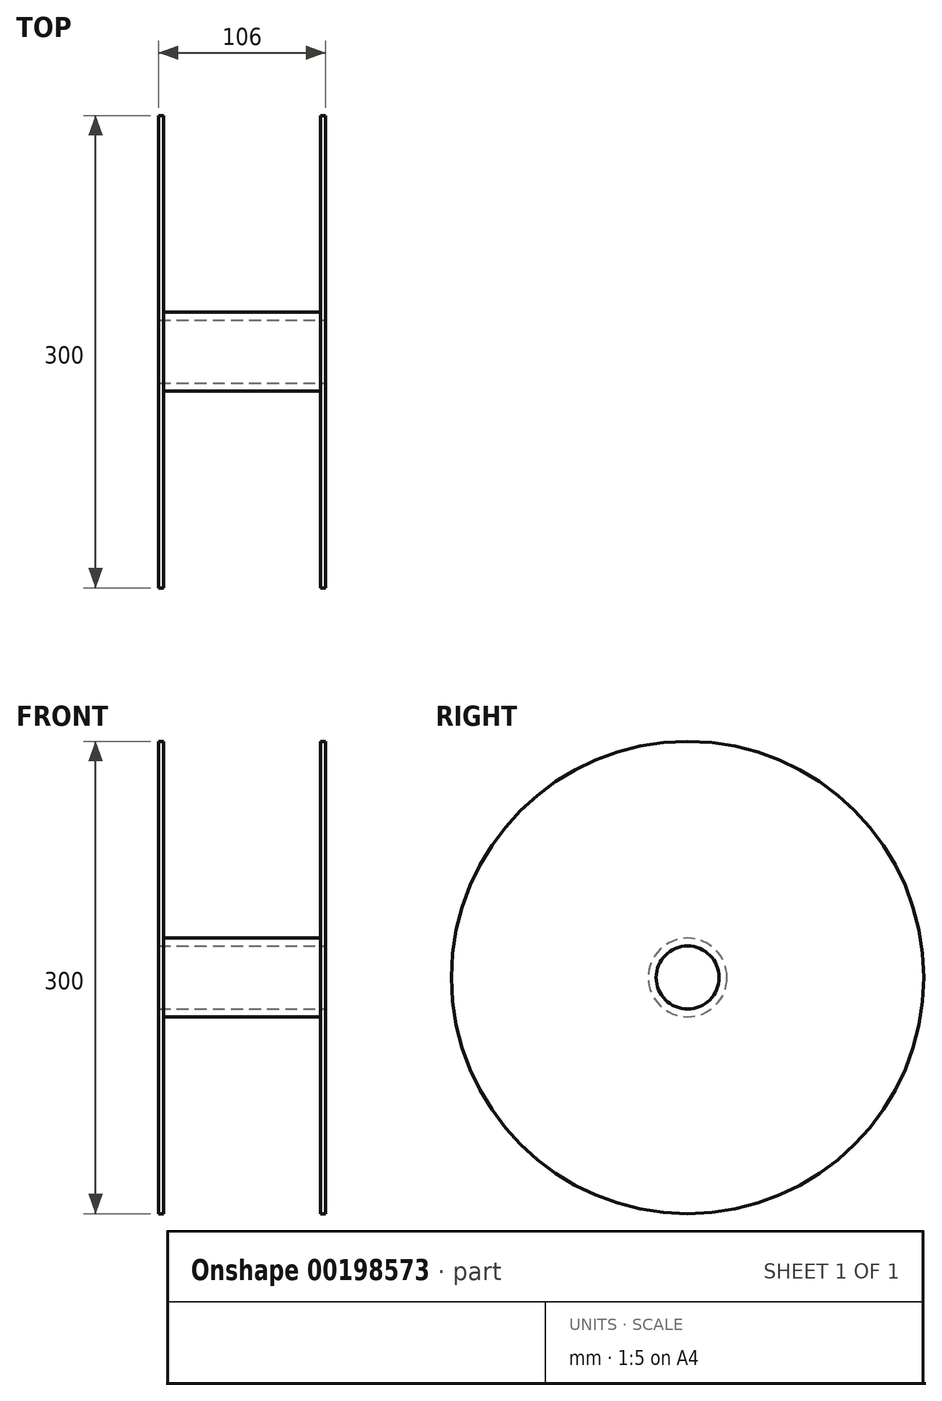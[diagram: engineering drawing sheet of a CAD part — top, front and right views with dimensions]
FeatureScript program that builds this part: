
annotation { "Feature Type Name" : "Feature", "Feature Type Description" : "" }
export const myFeature = defineFeature(function(context is Context, id is Id, definition is map)
    precondition{}
    {
        {
            var Q0;
            Q0=qCreatedBy(makeId("Front.planeOp"),FACE);
            var sketch = newSketch(context, id + "F0", { "sketchPlane" : qUnion([Q0])});
            skLineSegment(sketch, "E0", {"start": v(0, 25) * mm, "end": v(50, 25) * mm});
            skLineSegment(sketch, "E1", {"start": v(50, 25) * mm, "end": v(50, 150) * mm});
            skLineSegment(sketch, "E2", {"start": v(50, 150) * mm, "end": v(53, 150) * mm});
            skLineSegment(sketch, "E3", {"start": v(53, 150) * mm, "end": v(53, 0) * mm});
            skLineSegment(sketch, "E4", {"start": v(0, 0) * mm, "end": v(117.13, 0) * mm, "construction": true});
            skLineSegment(sketch, "E5", {"start": v(53, 0) * mm, "end": v(0, 0) * mm});
            skLineSegment(sketch, "E6", {"start": v(0, 25) * mm, "end": v(0, 87.4) * mm, "construction": true});
            skLineSegment(sketch, "E7.MirrorCS", {"start": v(-50, 150) * mm, "end": v(-53, 150) * mm});
            skLineSegment(sketch, "E8.MirrorCS", {"start": v(-53, 0) * mm, "end": v(0, 0) * mm});
            skLineSegment(sketch, "E9.MirrorCS", {"start": v(-53, 150) * mm, "end": v(-53, 0) * mm});
            skLineSegment(sketch, "E10.MirrorCS", {"start": v(0, 0) * mm, "end": v(-117.13, 0) * mm, "construction": true});
            skLineSegment(sketch, "E11.MirrorCS", {"start": v(-50, 25) * mm, "end": v(-50, 150) * mm});
            skLineSegment(sketch, "E12.MirrorCS", {"start": v(0, 25) * mm, "end": v(-50, 25) * mm});
            skSolve(sketch);
        }
        {
            var Q0;
            Q0 = qSketchRegion(id + "F0", true);
            var Q1;
            Q1=sQuery(id+"F0.wireOp",EDGE,"E4");
            revolve(context, id + "F1", {"entities" : qUnion([Q0]), "axis" : qUnion([Q1]), "revolveType" : RevolveType.FULL});
        }
        {
            var Q0;
            Q0=makeQuery(id+"F1.opRevolve","SWEPT_FACE",FACE,{"disambiguationData":[OSD([sQuery(id+"F0.wireOp",EDGE,"E3")])]});
            var sketch = newSketch(context, id + "F2", { "sketchPlane" : qUnion([Q0])});
            skPoint(sketch, "E13", {"position": v(0, 0) * mm});
            skSolve(sketch);
        }
        {
            var Q0;
            Q0=sQuery(id+"F2.wireOp",VERTEX,"E13");
            var Q1;
            Q1=makeQuery(id+"F1.opRevolve","SWEPT_BODY",BODY,{"disambiguationData":[OSD([sQuery(id+"F0.wireOp",EDGE,"E0"),sQuery(id+"F0.wireOp",EDGE,"E1"),sQuery(id+"F0.wireOp",EDGE,"E2"),sQuery(id+"F0.wireOp",EDGE,"E3"),sQuery(id+"F0.wireOp",EDGE,"E5"),sQuery(id+"F0.wireOp",EDGE,"E7.MirrorCS"),sQuery(id+"F0.wireOp",EDGE,"E8.MirrorCS"),sQuery(id+"F0.wireOp",EDGE,"E9.MirrorCS"),sQuery(id+"F0.wireOp",EDGE,"E11.MirrorCS"),sQuery(id+"F0.wireOp",EDGE,"E12.MirrorCS")])]});
            hole(context, id + "F3", {"style" : HoleStyle.SIMPLE, "endStyle" : HoleEndStyle.THROUGH, "holeDiameter" : 40 * mm, "startFromSketch" : true, "locations" : qUnion([Q0]), "scope" : qUnion([Q1]), "isTappedThrough" : true});
        }
    });
